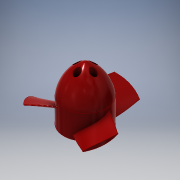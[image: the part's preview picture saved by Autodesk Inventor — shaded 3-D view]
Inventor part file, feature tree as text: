
AUTODESK INVENTOR PART (.ipt)
format: ipt  version: 2017 (Build 210142000, 142)  size: 525,824 bytes
history: native  units: mm
features: sketch x15, extrude x11, other x9, projected_geometry x5, plane x3, revolve x2, pattern_circular x2, loft x1, boolean_combine x1, fillet x1
ambient origin geometry x8: Origin, YZ Plane, XZ Plane, XY Plane, X Axis, Y Axis, Z Axis, Center Point
bodies: Body (feature_tree)
feature tree (50):
  other  "CrossSection1"
  other  "CrossSection2"
  other  "CrossSection3"
  other  "CrossSection4"
  other  "CrossSection5"
  other  "CrossSection6"
  other  "CrossSection7"
  extrude  "Extrusion1"  Depth=2.0mm
  revolve  "Revolution1"  Angle=90.0deg
  plane  "Work Plane2"
  sketch  "Sketch4"  dims[d6=40.0mm d7=1.0mm]
  plane  "Work Plane1"
  sketch  "Sketch5"  dims[d18=35.0mm]
  loft  "Loft1"
  pattern_circular  "Circular Pattern1"  Count=4  [1 undecoded]
  extrude  "Extrusion5"  Depth=21.7mm TaperAngle=0.0deg
  extrude  "Extrusion6"  Depth=2.5mm
  plane  "Work Plane3"
  extrude  "Extrusion7"  Depth=4.0mm TaperAngle=0.0deg
  extrude  "Extrusion8"  Depth=6.0mm
  extrude  "Extrusion9"  Depth=3.0mm TaperAngle=0.0deg
  pattern_circular  "Circular Pattern2"  [2 undecoded]
  extrude  "Extrusion10"  Depth=3.0mm TaperAngle=0.0deg
  extrude  "Extrusion11"  Depth=40.0mm TaperAngle=360.0deg
  boolean_combine  "Combine1"
  fillet  "Fillet2"  Radius=3.56mm
  extrude  "Extrusion12"  Depth=16.5mm TaperAngle=0.0deg
  extrude  "Extrusion13"  Depth=9.27mm
  extrude  "Extrusion14"  Depth=2.5mm TaperAngle=0.0deg
  revolve  "Revolution2"  [1 undecoded]
  sketch  "Sketch1"  dims[d0=28.1mm d1=2.0mm]
  sketch  "Sketch2"  dims[d2=18.0mm d3=0.0mm d5=90.0deg]
  projected_geometry  "Projected Loop1"
  projected_geometry  "Projected Loop2"
  other  "Cone"
  projected_geometry  "Projected Loop5"
  projected_geometry  "Projected Loop6"
  sketch  "Sketch7"  dims[d22=30.0deg]
  sketch  "Sketch8"  dims[d23=3.5mm]
  sketch  "Sketch9"  dims[d24=0.0mm d25=90.0deg d26=0.0mm d27=90.0deg d28=9.5mm]
  sketch  "Sketch10"  dims[d29=60.0deg]
  sketch  "Sketch11"  dims[d31=22.0mm]
  sketch  "Sketch12"  dims[d37=65.0mm]
  sketch  "Sketch13"  dims[d38=12.0mm d39=40.0mm d40=0.0mm]
  sketch  "Sketch14"  dims[d42=30.0mm d43=360.0deg d48=21.7mm d49=0.0mm]
  sketch  "Sketch15"  dims[d50=5.0mm d51=2.5mm]
  projected_geometry  "Projected Loop8"
  other  "Support"
  sketch  "Sketch16"  dims[d52=-21.7mm d53=4.0mm d54=0.0mm]
  sketch  "Sketch17"  dims[d58=2.5mm d59=6.0mm d60=3.0mm d61=0.0mm d62=4.8mm d63=3.0mm d64=0.0mm d65=40.0mm d66=360.0deg d68=3.56mm d69=16.5mm d70=0.0mm d71=9.27mm d72=2.5mm d73=0.0mm d74=0.5mm d75=2.0mm d76=-3.75mm d77=20.0mm d78=0.5mm d79=2.0mm d80=0.0mm d81=20.0mm d82=0.5mm d83=2.0mm d84=0.0mm d85=20.0mm d86=0.5mm d87=2.0mm d88=0.0mm d89=20.0mm d90=0.5mm d91=2.0mm d92=0.0mm d93=20.0mm d94=0.5mm d95=2.0mm d96=0.0mm d97=20.0mm d98=0.3mm d99=0.2mm d100=0.0mm d101=0.5mm d102=2.0mm d103=-23.0mm d104=20.0mm d105=0.2mm d106=0.0mm d107=0.2mm d108=0.0mm d112=6.981317mm d113=3.5mm d114=90.0deg]
note: 4 required parameter values undecoded (feature->parameter linkage not recoverable at this tier; creation-order binding heuristic only, values carry confidence <= 0.55)